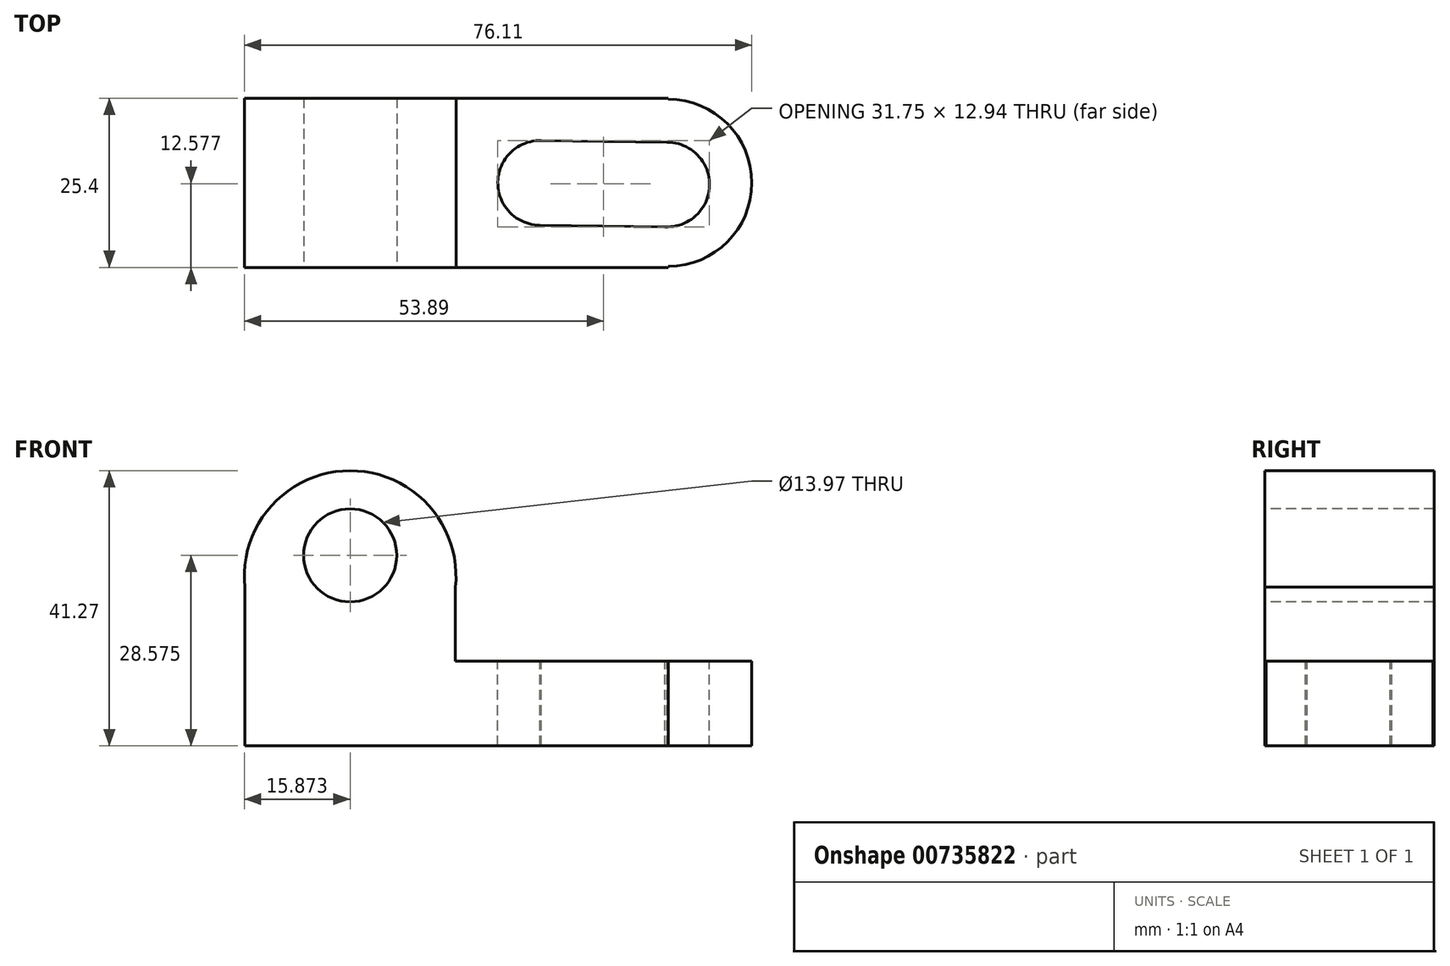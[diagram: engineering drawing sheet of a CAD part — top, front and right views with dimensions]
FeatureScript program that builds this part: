
annotation { "Feature Type Name" : "Feature", "Feature Type Description" : "" }
export const myFeature = defineFeature(function(context is Context, id is Id, definition is map)
    precondition{}
    {
        {
            var Q0;
            Q0=qCreatedBy(makeId("Top.planeOp"),FACE);
            var sketch = newSketch(context, id + "F0", { "sketchPlane" : qUnion([Q0])});
            skLineSegment(sketch, "E0", {"start": v(0, 0) * mm, "end": v(0, 25.4) * mm});
            skLineSegment(sketch, "E1", {"start": v(0, 25.4) * mm, "end": v(63.5, 25.4) * mm});
            skLineSegment(sketch, "E2", {"start": v(63.5, 25.4) * mm, "end": v(63.5, 0) * mm});
            skLineSegment(sketch, "E3", {"start": v(63.5, 0) * mm, "end": v(0, 0) * mm});
            skSolve(sketch);
        }
        {
            var Q0;
            Q0 = qSketchRegion(id + "F0", true);
            extrude(context, id + "F1", {"entities" : qUnion([Q0]), "depth" : 12.7 * mm, "offsetDistance" : 25.4 * mm});
        }
        {
            var Q0;
            Q0=makeQuery(id+"F1.opExtrude","CAP_FACE",FACE,{"disambiguationData":[OSD([sQuery(id+"F0.wireOp",EDGE,"E0"),sQuery(id+"F0.wireOp",EDGE,"E1"),sQuery(id+"F0.wireOp",EDGE,"E2"),sQuery(id+"F0.wireOp",EDGE,"E3")])],"isStart":false});
            var sketch = newSketch(context, id + "F2", { "sketchPlane" : qUnion([Q0])});
            skCircle(sketch, "E4", {"center": v(63.5, 12.7) * mm, "radius": 12.53 * mm});
            skSolve(sketch);
        }
        {
            var Q0;
            Q0 = qSketchRegion(id + "F2", true);
            extrude(context, id + "F3", {"entities" : qUnion([Q0]), "operationType" : NewBodyOperationType.ADD, "oppositeDirection" : true, "depth" : 12.7 * mm, "offsetDistance" : 25.4 * mm});
        }
        {
            var Q0;
            Q0=makeQuery(id+"F3.boolean.opBoolean","MERGE",FACE,{"derivedFrom":[makeQuery(id+"F1.opExtrude","CAP_FACE",FACE,{"disambiguationData":[OSD([sQuery(id+"F0.wireOp",EDGE,"E0"),sQuery(id+"F0.wireOp",EDGE,"E1"),sQuery(id+"F0.wireOp",EDGE,"E2"),sQuery(id+"F0.wireOp",EDGE,"E3")])],"isStart":false}),makeQuery(id+"F3.opExtrude","CAP_FACE",FACE,{"disambiguationData":[OSD([sQuery(id+"F2.wireOp",EDGE,"E4")])],"isStart":true})]});
            var sketch = newSketch(context, id + "F4", { "sketchPlane" : qUnion([Q0])});
            skCircle(sketch, "E5", {"center": v(63.33, 12.45) * mm, "radius": 6.35 * mm});
            skCircle(sketch, "E6", {"center": v(44.29, 12.7) * mm, "radius": 6.35 * mm});
            skLineSegment(sketch, "E7", {"start": v(44.29, 19.05) * mm, "end": v(63.33, 18.8) * mm});
            skLineSegment(sketch, "E8", {"start": v(63.33, 18.8) * mm, "end": v(63.5, 6.1) * mm});
            skLineSegment(sketch, "E9", {"start": v(63.5, 6.1) * mm, "end": v(44.29, 6.35) * mm});
            skLineSegment(sketch, "E10", {"start": v(44.29, 6.35) * mm, "end": v(44.29, 19.05) * mm});
            skSolve(sketch);
        }
        {
            var Q0;
            Q0 = qSketchRegion(id + "F4", true);
            extrude(context, id + "F5", {"entities" : qUnion([Q0]), "operationType" : NewBodyOperationType.REMOVE, "oppositeDirection" : true, "depth" : 12.7 * mm, "offsetDistance" : 25.4 * mm});
        }
        {
            var Q0;
            Q0=makeQuery(id+"F3.boolean.opBoolean","MERGE",FACE,{"derivedFrom":[makeQuery(id+"F1.opExtrude","CAP_FACE",FACE,{"disambiguationData":[OSD([sQuery(id+"F0.wireOp",EDGE,"E0"),sQuery(id+"F0.wireOp",EDGE,"E1"),sQuery(id+"F0.wireOp",EDGE,"E2"),sQuery(id+"F0.wireOp",EDGE,"E3")])],"isStart":false}),makeQuery(id+"F3.opExtrude","CAP_FACE",FACE,{"disambiguationData":[OSD([sQuery(id+"F2.wireOp",EDGE,"E4")])],"isStart":true})]});
            var sketch = newSketch(context, id + "F6", { "sketchPlane" : qUnion([Q0])});
            skLineSegment(sketch, "E11", {"start": v(0, 0) * mm, "end": v(0, 25.4) * mm});
            skLineSegment(sketch, "E12", {"start": v(0, 25.4) * mm, "end": v(31.59, 25.4) * mm});
            skLineSegment(sketch, "E13", {"start": v(31.59, 25.4) * mm, "end": v(31.59, 0) * mm});
            skLineSegment(sketch, "E14", {"start": v(31.59, 0) * mm, "end": v(0, 0) * mm});
            skSolve(sketch);
        }
        {
            var Q0;
            Q0 = qSketchRegion(id + "F6", true);
            extrude(context, id + "F7", {"entities" : qUnion([Q0]), "operationType" : NewBodyOperationType.ADD, "depth" : 12.7 * mm, "offsetDistance" : 25.4 * mm});
        }
        {
            var Q0;
            Q0=makeQuery(id+"F7.boolean.opBoolean","MERGE",FACE,{"derivedFrom":[makeQuery(id+"F1.opExtrude","SWEPT_FACE",FACE,{"disambiguationData":[OSD([sQuery(id+"F0.wireOp",EDGE,"E3")])]}),makeQuery(id+"F7.opExtrude","SWEPT_FACE",FACE,{"disambiguationData":[OSD([sQuery(id+"F6.wireOp",EDGE,"E14")])]})]});
            var sketch = newSketch(context, id + "F8", { "sketchPlane" : qUnion([Q0])});
            skCircle(sketch, "E15", {"center": v(15.8, 25.4) * mm, "radius": 15.88 * mm});
            skSolve(sketch);
        }
        {
            var Q0;
            Q0 = qSketchRegion(id + "F8", true);
            extrude(context, id + "F9", {"entities" : qUnion([Q0]), "operationType" : NewBodyOperationType.ADD, "oppositeDirection" : true, "depth" : 25.4 * mm, "offsetDistance" : 25.4 * mm});
        }
        {
            var Q0;
            Q0=makeQuery(id+"F9.boolean.opBoolean","MERGE",FACE,{"derivedFrom":[makeQuery(id+"F7.boolean.opBoolean","MERGE",FACE,{"derivedFrom":[makeQuery(id+"F1.opExtrude","SWEPT_FACE",FACE,{"disambiguationData":[OSD([sQuery(id+"F0.wireOp",EDGE,"E3")])]}),makeQuery(id+"F7.opExtrude","SWEPT_FACE",FACE,{"disambiguationData":[OSD([sQuery(id+"F6.wireOp",EDGE,"E14")])]})]}),makeQuery(id+"F9.opExtrude","CAP_FACE",FACE,{"disambiguationData":[OSD([sQuery(id+"F8.wireOp",EDGE,"E15")])],"isStart":true})]});
            var sketch = newSketch(context, id + "F10", { "sketchPlane" : qUnion([Q0])});
            skCircle(sketch, "E16", {"center": v(15.8, 28.58) * mm, "radius": 6.99 * mm});
            skSolve(sketch);
        }
        {
            var Q0;
            Q0 = qSketchRegion(id + "F10", true);
            extrude(context, id + "F11", {"entities" : qUnion([Q0]), "operationType" : NewBodyOperationType.REMOVE, "oppositeDirection" : true, "depth" : 25.4 * mm, "offsetDistance" : 25.4 * mm});
        }
    });
